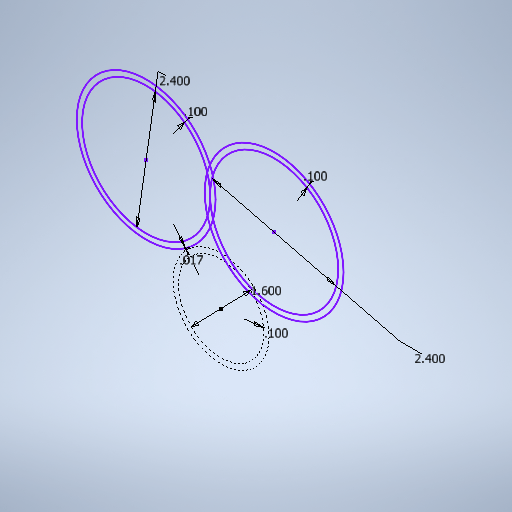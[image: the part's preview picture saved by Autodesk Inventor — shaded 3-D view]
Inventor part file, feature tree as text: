
AUTODESK INVENTOR PART (.ipt)
format: ipt  version: 2025.1 (Build 291241020, 241B)  size: 265,728 bytes
history: native  units: in
note: dims shown in document units (in); Inventor stores cm internally (conversion verified against a paired STEP export)
features: sketch x1
ambient origin geometry x8: Origin, YZ Plane, XZ Plane, XY Plane, X Axis, Y Axis, Z Axis, Center Point
feature tree (1):
  sketch  "Sketch1"  dims[d0=1.6in d2=2.4in d3=0.1in d4=0.1in d6=0.1in d7=2.4in d8=0.0167in]
